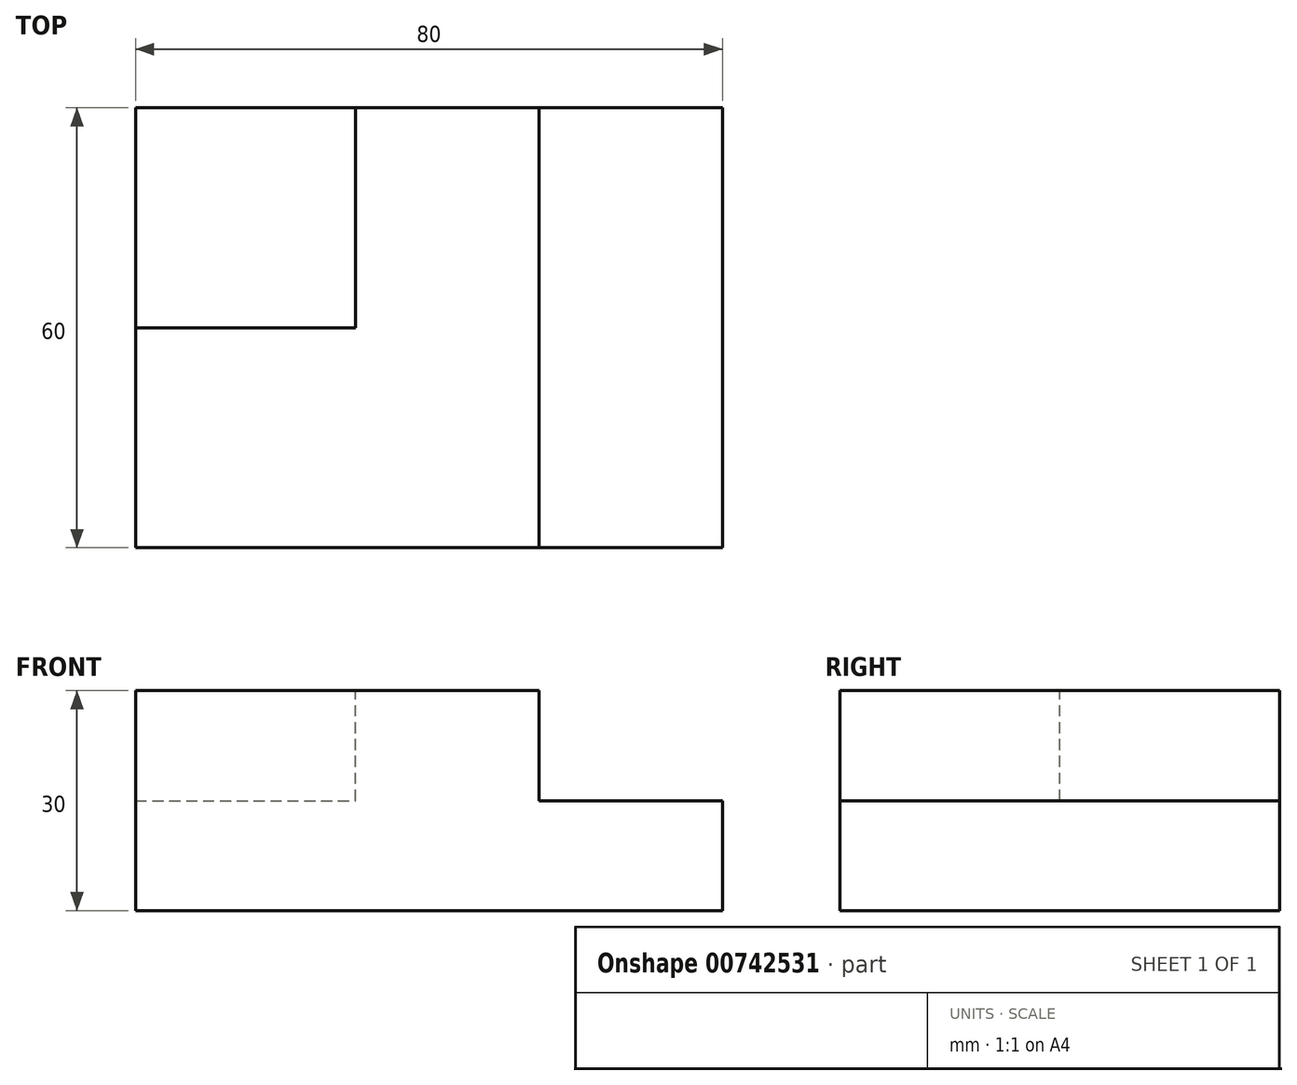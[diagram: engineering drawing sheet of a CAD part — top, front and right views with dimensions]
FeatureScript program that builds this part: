
annotation { "Feature Type Name" : "Feature", "Feature Type Description" : "" }
export const myFeature = defineFeature(function(context is Context, id is Id, definition is map)
    precondition{}
    {
        {
            var Q0;
            Q0=qCreatedBy(makeId("Top.planeOp"),FACE);
            var sketch = newSketch(context, id + "F0", { "sketchPlane" : qUnion([Q0])});
            skLineSegment(sketch, "E0.bottom", {"start": v(0, 0) * mm, "end": v(80, 0) * mm});
            skLineSegment(sketch, "E0.top", {"start": v(0, 60) * mm, "end": v(80, 60) * mm});
            skLineSegment(sketch, "E0.left", {"start": v(0, 0) * mm, "end": v(0, 60) * mm});
            skLineSegment(sketch, "E0.right", {"start": v(80, 0) * mm, "end": v(80, 60) * mm});
            skLineSegment(sketch, "E1.bottom", {"start": v(0, 60) * mm, "end": v(30, 60) * mm});
            skLineSegment(sketch, "E1.top", {"start": v(0, 30) * mm, "end": v(30, 30) * mm});
            skLineSegment(sketch, "E1.left", {"start": v(0, 60) * mm, "end": v(0, 30) * mm});
            skLineSegment(sketch, "E1.right", {"start": v(30, 60) * mm, "end": v(30, 30) * mm});
            skLineSegment(sketch, "E2.bottom", {"start": v(80, 60) * mm, "end": v(55, 60) * mm});
            skLineSegment(sketch, "E2.top", {"start": v(80, 0) * mm, "end": v(55, 0) * mm});
            skLineSegment(sketch, "E2.left", {"start": v(80, 60) * mm, "end": v(80, 0) * mm});
            skLineSegment(sketch, "E2.right", {"start": v(55, 60) * mm, "end": v(55, 0) * mm});
            skSolve(sketch);
        }
        {
            var Q0;
            {var subQ0=sQuery(id+"F0.wireOp",EDGE,"E1.top");Q0=makeQuery(id+"F0.imprint","IMPRINT",FACE,{"disambiguationData":[TD([[makeQuery(id+"F0.imprint","IMPRINT",EDGE,{"derivedFrom":subQ0}),-1.0]])]});}
            var Q1;
            {var subQ4=sQuery(id+"F0.wireOp",EDGE,"E1.top");Q1=makeQuery(id+"F0.imprint","IMPRINT",FACE,{"disambiguationData":[TD([[makeQuery(id+"F0.imprint","IMPRINT",EDGE,{"derivedFrom":subQ4}),1.0]])]});}
            var Q2;
            {var subQ0=sQuery(id+"F0.wireOp",EDGE,"E0.right");Q2=makeQuery(id+"F0.imprint","IMPRINT",FACE,{"disambiguationData":[TD([[makeQuery(id+"F0.imprint","IMPRINT",EDGE,{"derivedFrom":subQ0}),1.0]])]});}
            extrude(context, id + "F1", {"entities" : qUnion([Q0, Q1, Q2]), "depth" : 30 * mm, "offsetDistance" : 25 * mm});
        }
        {
            var Q0;
            Q0=makeQuery(id+"F1.opExtrude","CAP_FACE",FACE,{"disambiguationData":[OSD([sQuery(id+"F0.wireOp",EDGE,"E0.bottom"),sQuery(id+"F0.wireOp",EDGE,"E0.top"),sQuery(id+"F0.wireOp",EDGE,"E0.left"),sQuery(id+"F0.wireOp",EDGE,"E0.right")])],"isStart":false});
            var sketch = newSketch(context, id + "F2", { "sketchPlane" : qUnion([Q0])});
            skLineSegment(sketch, "E3.bottom", {"start": v(0, 60) * mm, "end": v(30, 60) * mm});
            skLineSegment(sketch, "E3.top", {"start": v(0, 30) * mm, "end": v(30, 30) * mm});
            skLineSegment(sketch, "E3.left", {"start": v(0, 60) * mm, "end": v(0, 30) * mm});
            skLineSegment(sketch, "E3.right", {"start": v(30, 60) * mm, "end": v(30, 30) * mm});
            skLineSegment(sketch, "E4.bottom", {"start": v(80, 60) * mm, "end": v(55, 60) * mm});
            skLineSegment(sketch, "E4.top", {"start": v(80, 0) * mm, "end": v(55, 0) * mm});
            skLineSegment(sketch, "E4.left", {"start": v(80, 60) * mm, "end": v(80, 0) * mm});
            skLineSegment(sketch, "E4.right", {"start": v(55, 60) * mm, "end": v(55, 0) * mm});
            skSolve(sketch);
        }
        {
            var Q0;
            Q0 = qSketchRegion(id + "F2", true);
            extrude(context, id + "F3", {"entities" : qUnion([Q0]), "operationType" : NewBodyOperationType.REMOVE, "oppositeDirection" : true, "depth" : 15 * mm, "offsetDistance" : 25 * mm});
        }
    });
